# Revit family: NBS_Allermuir_DmstcChrs_Mote_Ottoman-MTE-OT120
name_source: partatom
category: Furniture
revit_build: Autodesk Revit 2016 (Build: 20161004_0715(x64)
units: mm (PartAtom-declared; Revit-internal decimal feet)

## family parameters
Always vertical = Yes
Cut with Voids When Loaded = No
Room Calculation Point = No
Shared = No
Work Plane-Based = No

## types (1)
- MTE-OT120
    AssetType = Moveable
    BIMObjectName = NBS_Allermuir_DomesticChairs_Mote_MTE-OT120
    Category = Pr_40_50_12_22:Dining chairs
    Depth = 750 mm
    Description = 120° ottoman
    DurationUnit = year
    ExpectedLife = 5
    Features = Fully upholstered, cast aluminium legs and aluminium perimeter frame finished in black powder coat, plastic glides with leveling adjustment, aluminium frame available in flint grey, mineral sand, mellow yellow or orange crush powder coat, two-tone upholstery
    FrameColourOptions = Flint grey, mineral sand, mellow yellow, orange crush
    FrameHeight = 246 mm  [stored 0.807087 ft]
    FrameMountingMaterial = NBS_Concept
    FramesColour = Black
    FramesFinish = Powder coat
    FramesMaterial = Aluminium
    HighestSeatingHeight = 0 mm  [stored 0 ft]
    IfcExportAs = IfcFurnitureType
    IfcExportType = SOFA
    IsBuiltIn = No
    LowestSeatingHeight = 0 mm  [stored 0 ft]
    ManufacturerName = Allermuir
    ManufacturerURL = http://www.thesenatorgroup.com
    ModelNumber = MTE-OT120
    ModelReference = Mote ottoman
    NBSCertification = www.nationalbimlibrary.com/cert/4aakrizm
    NBSDescription = Domestic chairs
    NBSReference = 45-35-20/365
    Name = DomesticChairs_Mote_MTE-OT120_Allermuir
    NominalDepth = 2040 mm
    NominalHeight = 470 mm
    NominalLength = 1030 mm
    NominalWidth = 2040 mm
    OptionalAccessories = 1 x front facing frame intergrated power unit with 2 x powered USB and 1 x power socket, 2 x rear facing frame intergrated power unit with 2 x powered USB and 1 x power socket
    ProductInformation = http://www.thesenatorgroup.com
    SeatAngle = 120.00°
    SeatArmRestHeight = 604 mm  [stored 1.98163 ft]
    SeatEndRestOffset = 65 mm
    SeatFrameMaterial = NBS_Concept
    SeatFrameWidth = 50 mm  [stored 0.164042 ft]
    SeatLegOffset = 165 mm
    SeatOverallWidth = 2130 mm
    SeatPowerSupplyMaterial = NBS_Concept
    SeatScreenHeight = 1325 mm  [stored 4.34711 ft]
    SeatingArmRestMaterial = NBS_Concept
    SeatingHeight = 468 mm  [stored 1.53543 ft]
    SeatingSeatMaterial = NBS_Concept
    SeatsAndBacksFinish = Two-tone upholstery available
    SeatsAndBacksMaterial = Upholstered
    Size = 2040 x 1130 x 470 mm
    Status = UNSET
    Uniclass2015Code = Pr_40_50_12_22
    Uniclass2015Title = Dining chairs
    Uniclass2015Version = Products v1.9
    Version = 1
    WarrantyDescription = Allermuir warrant that its manufactured products are free from manufacturing defects in materials or workmanship for a period of five years
    WarrantyDurationParts = 5
    WarrantyDurationUnit = year

note: [stored X ft] marks values corroborated as IEEE doubles in the binary element streams (Revit-internal decimal feet)

## geometry (parser evidence)
native form markers: Sweep x9
no freeform markers — native parametric forms only
